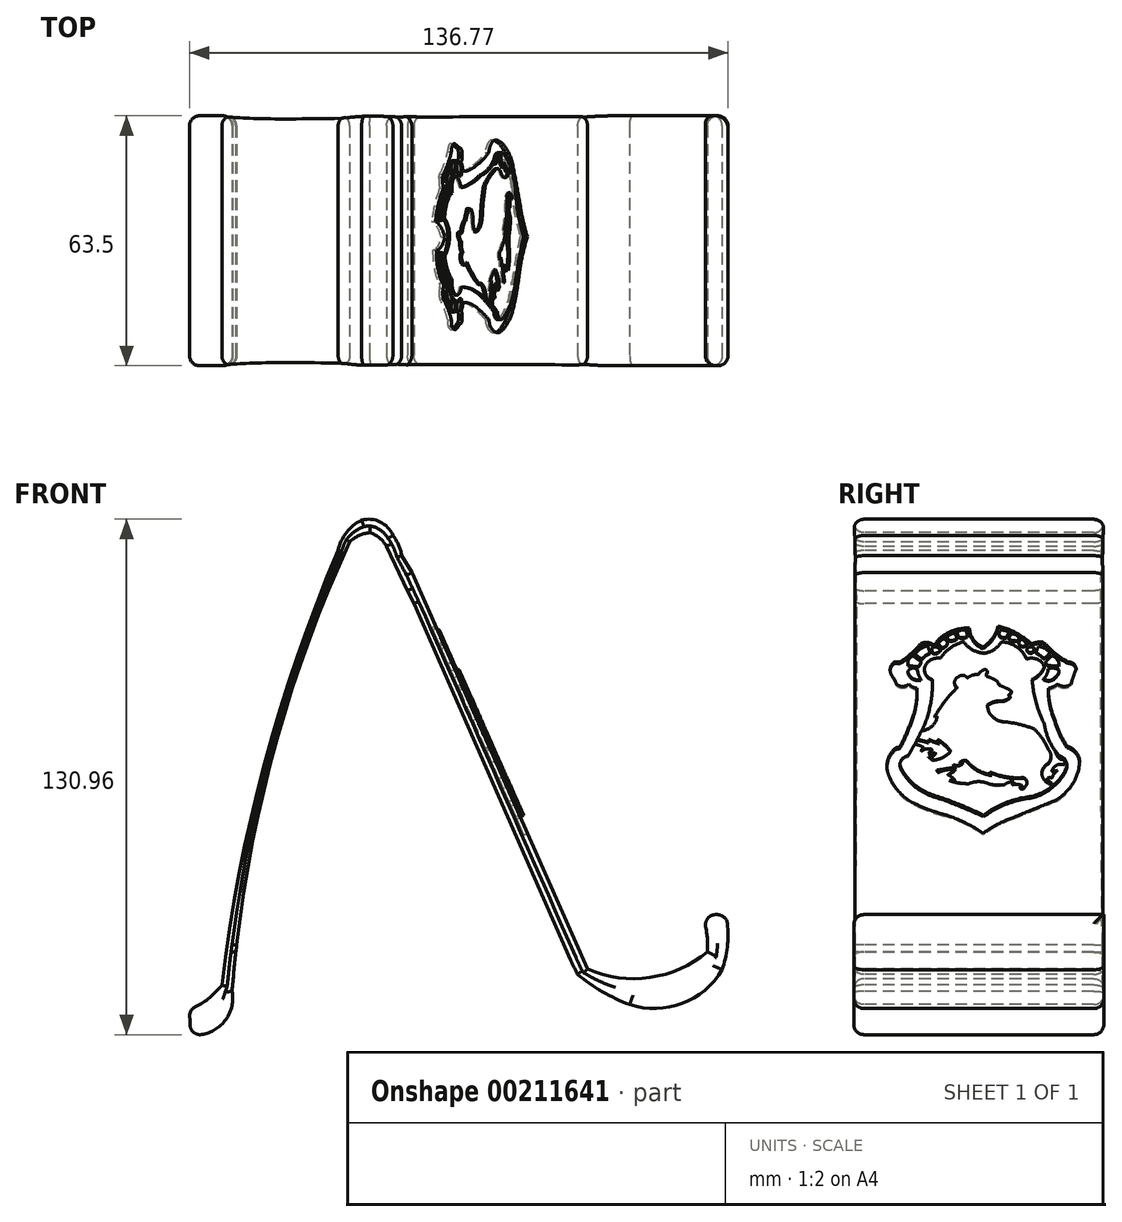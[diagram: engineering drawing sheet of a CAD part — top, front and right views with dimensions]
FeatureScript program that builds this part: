
annotation { "Feature Type Name" : "Feature", "Feature Type Description" : "" }
export const myFeature = defineFeature(function(context is Context, id is Id, definition is map)
    precondition{}
    {
        {
            var Q0;
            Q0=qCreatedBy(makeId("Front.planeOp"),FACE);
            var sketch = newSketch(context, id + "F0", { "sketchPlane" : qUnion([Q0])});
            skArc(sketch, "E0", {"start": v(-97.52, -51.49) * mm, "mid": v(-88.98, -49.1) * mm, "end": v(-86.27, -40.67) * mm});
            skArc(sketch, "E1", {"start": v(-56.41, 73.57) * mm, "mid": v(-76.4, 17.77) * mm, "end": v(-86.27, -40.67) * mm});
            skArc(sketch, "E2", {"start": v(-42.13, 67.94) * mm, "mid": v(-42.15, 68.13) * mm, "end": v(-42.16, 68.32) * mm});
            skArc(sketch, "E3", {"start": v(-0.28, -32.63) * mm, "mid": v(17.43, -37.36) * mm, "end": v(34.47, -30.58) * mm});
            skArc(sketch, "E4", {"start": v(34.47, -30.58) * mm, "mid": v(34.32, -25.84) * mm, "end": v(33.22, -21.21) * mm});
            skArc(sketch, "E5", {"start": v(39.25, -21.21) * mm, "mid": v(36.23, -21.14) * mm, "end": v(33.22, -21.21) * mm});
            skArc(sketch, "E6", {"start": v(1.53, -36.3) * mm, "mid": v(7.8, -40.71) * mm, "end": v(14.75, -44) * mm});
            skArc(sketch, "E7", {"start": v(-97.56, -45.4) * mm, "mid": v(-88.86, -39) * mm, "end": v(-85.13, -28.86) * mm});
            skArc(sketch, "E8", {"start": v(-97.52, -51.49) * mm, "mid": v(-96.94, -48.44) * mm, "end": v(-97.56, -45.4) * mm});
            skArc(sketch, "E9", {"start": v(-53.37, 79.07) * mm, "mid": v(-57.25, 75.9) * mm, "end": v(-59.32, 71.35) * mm});
            skArc(sketch, "E10", {"start": v(-59.32, 71.35) * mm, "mid": v(-78.06, 17.24) * mm, "end": v(-88.86, -39) * mm});
            skLineSegment(sketch, "E11", {"start": v(-97.52, -51.49) * mm, "end": v(-93.4, -51.49) * mm});
            skLineSegment(sketch, "E12", {"start": v(-86.19, -41.21) * mm, "end": v(-86.27, -40.67) * mm});
            skArc(sketch, "E13", {"start": v(38.22, -35.16) * mm, "mid": v(39.62, -28.25) * mm, "end": v(39.25, -21.21) * mm});
            skPoint(sketch, "E14.center.orphan", {"position": v(-0.28, -34.03) * mm});
            skPoint(sketch, "E15.start.orphan", {"position": v(39.25, -46.85) * mm});
            skArc(sketch, "E16", {"start": v(14.75, -44) * mm, "mid": v(28.05, -43.73) * mm, "end": v(38.22, -35.16) * mm});
            skPoint(sketch, "E17.orphan", {"position": v(30.56, -46.85) * mm});
            skLineSegment(sketch, "E18", {"start": v(-40.62, 65.75) * mm, "end": v(4, -34.96) * mm});
            skLineSegment(sketch, "E19", {"start": v(4, -34.96) * mm, "end": v(-0.28, -34.03) * mm});
            skLineSegment(sketch, "E20", {"start": v(-40.1, 57.85) * mm, "end": v(-0.28, -32.63) * mm});
            skArc(sketch, "E21", {"start": v(-0.28, -32.63) * mm, "mid": v(0.58, -34.49) * mm, "end": v(1.53, -36.3) * mm});
            skLineSegment(sketch, "E22", {"start": v(-41.73, 61.14) * mm, "end": v(-40.1, 57.85) * mm});
            skLineSegment(sketch, "E23", {"start": v(-41.73, 61.14) * mm, "end": v(-47.04, 72.42) * mm});
            skArc(sketch, "E24", {"start": v(-46.65, 71.6) * mm, "mid": v(-48.5, 74.28) * mm, "end": v(-51.32, 75.9) * mm});
            skPoint(sketch, "E25.orphan", {"position": v(-48.57, 75.7) * mm});
            skArc(sketch, "E26.trimOffspring", {"start": v(-51.32, 75.9) * mm, "mid": v(-54.06, 75.17) * mm, "end": v(-56.41, 73.57) * mm});
            skPoint(sketch, "E27.orphan", {"position": v(-59.32, 67.09) * mm});
            skArc(sketch, "E28", {"start": v(-45.43, 75.19) * mm, "mid": v(-48.66, 78.64) * mm, "end": v(-53.37, 79.07) * mm});
            skLineSegment(sketch, "E29.trimOffspring", {"start": v(-43.2, 70.06) * mm, "end": v(-40.62, 65.75) * mm});
            skPoint(sketch, "E30.orphan", {"position": v(-49.27, 80.15) * mm});
            skArc(sketch, "E31", {"start": v(-43.2, 70.06) * mm, "mid": v(-43.98, 72.77) * mm, "end": v(-45.43, 75.19) * mm});
            skPoint(sketch, "E32.orphan", {"position": v(-44.95, 72.95) * mm});
            skSolve(sketch);
        }
        {
            var Q0;
            Q0 = qSketchRegion(id + "F0", true);
            extrude(context, id + "F1", {"entities" : qUnion([Q0]), "oppositeDirection" : true, "depth" : 63.5 * mm});
        }
        {
            var Q0;
            Q0=makeQuery(id+"F1.opExtrude","SWEPT_FACE",FACE,{"disambiguationData":[OSD([sQuery(id+"F0.wireOp",EDGE,"E18")])]});
            var sketch = newSketch(context, id + "F2", { "sketchPlane" : qUnion([Q0])});
            skArc(sketch, "E33", {"start": v(29.4, 61.13) * mm, "mid": v(30.3, 58.01) * mm, "end": v(32.73, 55.87) * mm});
            skArc(sketch, "E34", {"start": v(32.73, 55.87) * mm, "mid": v(35.27, 58.44) * mm, "end": v(36.65, 61.78) * mm});
            skArc(sketch, "E35", {"start": v(45.1, 56.77) * mm, "mid": v(41.2, 59.83) * mm, "end": v(36.65, 61.78) * mm});
            skArc(sketch, "E36", {"start": v(47.95, 57.36) * mm, "mid": v(46.5, 57.23) * mm, "end": v(45.1, 56.77) * mm});
            skArc(sketch, "E37", {"start": v(47.95, 57.36) * mm, "mid": v(48.28, 56.98) * mm, "end": v(48.73, 56.77) * mm});
            skArc(sketch, "E38", {"start": v(48.73, 56.77) * mm, "mid": v(51.3, 53.95) * mm, "end": v(54.45, 51.76) * mm});
            skArc(sketch, "E39", {"start": v(56.47, 49.71) * mm, "mid": v(55.9, 51.16) * mm, "end": v(54.45, 51.76) * mm});
            skArc(sketch, "E40", {"start": v(56.47, 49.71) * mm, "mid": v(55.74, 47.66) * mm, "end": v(55.15, 45.55) * mm});
            skArc(sketch, "E41", {"start": v(51.75, 45.55) * mm, "mid": v(53.45, 44.95) * mm, "end": v(55.15, 45.55) * mm});
            skArc(sketch, "E42", {"start": v(49.39, 44.38) * mm, "mid": v(50.62, 44.87) * mm, "end": v(51.75, 45.55) * mm});
            skArc(sketch, "E43", {"start": v(49.39, 44.38) * mm, "mid": v(49.78, 40.1) * mm, "end": v(50.94, 35.98) * mm});
            skArc(sketch, "E44", {"start": v(50.94, 35.98) * mm, "mid": v(52.27, 32.04) * mm, "end": v(54.13, 28.34) * mm});
            skArc(sketch, "E45", {"start": v(57.36, 24.3) * mm, "mid": v(56.36, 26.81) * mm, "end": v(54.13, 28.34) * mm});
            skArc(sketch, "E46", {"start": v(51.39, 13.37) * mm, "mid": v(55.7, 18.12) * mm, "end": v(57.36, 24.3) * mm});
            skArc(sketch, "E47", {"start": v(51.39, 13.37) * mm, "mid": v(46, 10.96) * mm, "end": v(40.6, 8.54) * mm});
            skArc(sketch, "E48", {"start": v(40.6, 8.54) * mm, "mid": v(36.52, 6.66) * mm, "end": v(32.85, 4.1) * mm});
            skArc(sketch, "E49", {"start": v(32.85, 4.1) * mm, "mid": v(28.39, 7) * mm, "end": v(23.53, 9.18) * mm});
            skArc(sketch, "E50", {"start": v(15.99, 12.12) * mm, "mid": v(19.68, 10.46) * mm, "end": v(23.53, 9.18) * mm});
            skArc(sketch, "E51", {"start": v(9.07, 19.72) * mm, "mid": v(11.8, 15.25) * mm, "end": v(15.99, 12.12) * mm});
            skArc(sketch, "E52", {"start": v(10.14, 27.4) * mm, "mid": v(8.45, 23.73) * mm, "end": v(9.07, 19.72) * mm});
            skArc(sketch, "E53", {"start": v(11.62, 28) * mm, "mid": v(10.8, 27.9) * mm, "end": v(10.14, 27.4) * mm});
            skArc(sketch, "E54", {"start": v(11.62, 28) * mm, "mid": v(13.53, 32.42) * mm, "end": v(15.1, 36.97) * mm});
            skArc(sketch, "E55", {"start": v(15.1, 36.97) * mm, "mid": v(15.89, 40.68) * mm, "end": v(15.99, 44.46) * mm});
            skArc(sketch, "E56", {"start": v(13.98, 45.57) * mm, "mid": v(14.89, 44.84) * mm, "end": v(15.99, 44.46) * mm});
            skArc(sketch, "E57", {"start": v(10.77, 45.57) * mm, "mid": v(12.38, 44.96) * mm, "end": v(13.98, 45.57) * mm});
            skArc(sketch, "E58", {"start": v(10.77, 45.57) * mm, "mid": v(10.36, 46.75) * mm, "end": v(9.72, 47.84) * mm});
            skArc(sketch, "E59", {"start": v(10.14, 51.67) * mm, "mid": v(9.22, 49.83) * mm, "end": v(9.72, 47.84) * mm});
            skArc(sketch, "E60", {"start": v(11.62, 51.67) * mm, "mid": v(10.88, 51.75) * mm, "end": v(10.14, 51.67) * mm});
            skArc(sketch, "E61", {"start": v(11.62, 51.67) * mm, "mid": v(14.5, 54) * mm, "end": v(16.94, 56.82) * mm});
            skArc(sketch, "E62", {"start": v(19.78, 56.82) * mm, "mid": v(18.36, 57.21) * mm, "end": v(16.94, 56.82) * mm});
            skArc(sketch, "E63", {"start": v(19.78, 56.82) * mm, "mid": v(20.52, 56.62) * mm, "end": v(20.95, 57.25) * mm});
            skArc(sketch, "E64", {"start": v(29.4, 61.13) * mm, "mid": v(24.69, 60.24) * mm, "end": v(20.95, 57.25) * mm});
            skSolve(sketch);
        }
        {
            var Q0;
            Q0=makeQuery(id+"F2.imprint","IMPRINT",FACE,{"disambiguationData":[TD([[makeQuery(id+"F2.imprint","IMPRINT",EDGE,{"derivedFrom":sQuery(id+"F2.wireOp",EDGE,"E33")}),-1.0]])]});
            extrude(context, id + "F3", {"entities" : qUnion([Q0]), "operationType" : NewBodyOperationType.REMOVE, "oppositeDirection" : true, "depth" : 1.02 * mm});
        }
        {
            var Q0;
            Q0=makeQuery(id+"F2.imprint","IMPRINT",FACE,{"disambiguationData":[TD([[makeQuery(id+"F2.imprint","IMPRINT",EDGE,{"derivedFrom":sQuery(id+"F2.wireOp",EDGE,"E33")}),-1.0]])]});
            var sketch = newSketch(context, id + "F4", { "sketchPlane" : qUnion([Q0])});
            skArc(sketch, "E65", {"start": v(22, 52.6) * mm, "mid": v(19.59, 52.1) * mm, "end": v(18.03, 50.19) * mm});
            skArc(sketch, "E66", {"start": v(18.03, 50.19) * mm, "mid": v(18.29, 48.04) * mm, "end": v(19.95, 46.66) * mm});
            skArc(sketch, "E67", {"start": v(18.03, 34.27) * mm, "mid": v(19.57, 40.37) * mm, "end": v(19.95, 46.66) * mm});
            skArc(sketch, "E68", {"start": v(13.75, 25.22) * mm, "mid": v(16.01, 29.68) * mm, "end": v(18.03, 34.27) * mm});
            skArc(sketch, "E69", {"start": v(13.75, 25.22) * mm, "mid": v(11.99, 24) * mm, "end": v(12, 21.87) * mm});
            skArc(sketch, "E70", {"start": v(12, 21.87) * mm, "mid": v(15.77, 16.9) * mm, "end": v(21.26, 13.94) * mm});
            skArc(sketch, "E71", {"start": v(32.96, 8.68) * mm, "mid": v(27.2, 11.5) * mm, "end": v(21.26, 13.94) * mm});
            skArc(sketch, "E72", {"start": v(45.27, 13.94) * mm, "mid": v(38.72, 12.24) * mm, "end": v(32.96, 8.68) * mm});
            skArc(sketch, "E73", {"start": v(45.27, 13.94) * mm, "mid": v(50.53, 16.91) * mm, "end": v(53.98, 21.87) * mm});
            skArc(sketch, "E74", {"start": v(53.98, 21.87) * mm, "mid": v(53.84, 23.93) * mm, "end": v(52.22, 25.22) * mm});
            skArc(sketch, "E75", {"start": v(48.38, 34.27) * mm, "mid": v(49.7, 29.5) * mm, "end": v(52.22, 25.22) * mm});
            skArc(sketch, "E76", {"start": v(45.27, 46.66) * mm, "mid": v(46.28, 40.33) * mm, "end": v(48.38, 34.27) * mm});
            skArc(sketch, "E77", {"start": v(45.27, 46.66) * mm, "mid": v(47.15, 48.14) * mm, "end": v(48.38, 50.19) * mm});
            skArc(sketch, "E78", {"start": v(48.38, 50.19) * mm, "mid": v(46.61, 52.25) * mm, "end": v(43.9, 52.32) * mm});
            skArc(sketch, "E79", {"start": v(43.9, 52.32) * mm, "mid": v(41.37, 55.7) * mm, "end": v(37.41, 57.14) * mm});
            skArc(sketch, "E80", {"start": v(32.96, 53.95) * mm, "mid": v(35.6, 54.97) * mm, "end": v(37.41, 57.14) * mm});
            skArc(sketch, "E81", {"start": v(27.87, 57.14) * mm, "mid": v(30.05, 54.97) * mm, "end": v(32.96, 53.95) * mm});
            skArc(sketch, "E82", {"start": v(27.87, 57.14) * mm, "mid": v(24.5, 55.42) * mm, "end": v(22, 52.6) * mm});
            skArc(sketch, "E83", {"start": v(13.75, 48.96) * mm, "mid": v(14.81, 47) * mm, "end": v(17.03, 46.66) * mm});
            skArc(sketch, "E84", {"start": v(16.12, 49.45) * mm, "mid": v(14.81, 49.77) * mm, "end": v(13.75, 48.96) * mm});
            skArc(sketch, "E85", {"start": v(16.12, 49.45) * mm, "mid": v(16.42, 48) * mm, "end": v(17.03, 46.66) * mm});
            skArc(sketch, "E86", {"start": v(13.75, 50.6) * mm, "mid": v(15, 50.35) * mm, "end": v(16.25, 50.19) * mm});
            skArc(sketch, "E87", {"start": v(15.05, 53.2) * mm, "mid": v(16.02, 52.43) * mm, "end": v(17.03, 51.7) * mm});
            skArc(sketch, "E88", {"start": v(16.25, 50.19) * mm, "mid": v(16.8, 50.86) * mm, "end": v(17.03, 51.7) * mm});
            skArc(sketch, "E89", {"start": v(15.05, 53.2) * mm, "mid": v(13.9, 52.15) * mm, "end": v(13.75, 50.6) * mm});
            skArc(sketch, "E90", {"start": v(15.64, 53.95) * mm, "mid": v(16.35, 52.98) * mm, "end": v(17.36, 52.32) * mm});
            skArc(sketch, "E91", {"start": v(19.32, 53.95) * mm, "mid": v(19.07, 55) * mm, "end": v(18.7, 56) * mm});
            skArc(sketch, "E92", {"start": v(18.7, 56) * mm, "mid": v(17.02, 55.21) * mm, "end": v(15.64, 53.95) * mm});
            skArc(sketch, "E93", {"start": v(19.32, 53.95) * mm, "mid": v(18.17, 53.35) * mm, "end": v(17.36, 52.32) * mm});
            skArc(sketch, "E94", {"start": v(22, 54.78) * mm, "mid": v(21.13, 55.58) * mm, "end": v(19.95, 55.47) * mm});
            skArc(sketch, "E95", {"start": v(19.95, 55.47) * mm, "mid": v(19.8, 54.83) * mm, "end": v(19.95, 54.2) * mm});
            skArc(sketch, "E96", {"start": v(20.86, 53.95) * mm, "mid": v(21.49, 54.3) * mm, "end": v(22, 54.78) * mm});
            skArc(sketch, "E97", {"start": v(19.95, 54.2) * mm, "mid": v(20.37, 53.94) * mm, "end": v(20.86, 53.95) * mm});
            skArc(sketch, "E98", {"start": v(21.49, 56.69) * mm, "mid": v(21.9, 55.98) * mm, "end": v(22.54, 55.47) * mm});
            skArc(sketch, "E99", {"start": v(22.54, 55.47) * mm, "mid": v(23.45, 56.1) * mm, "end": v(23.82, 57.14) * mm});
            skArc(sketch, "E100", {"start": v(22.98, 57.93) * mm, "mid": v(22.09, 57.48) * mm, "end": v(21.49, 56.69) * mm});
            skArc(sketch, "E101", {"start": v(22.98, 57.93) * mm, "mid": v(23.4, 57.52) * mm, "end": v(23.82, 57.14) * mm});
            skArc(sketch, "E102", {"start": v(23.82, 58.6) * mm, "mid": v(23.94, 57.87) * mm, "end": v(24.55, 57.45) * mm});
            skArc(sketch, "E103", {"start": v(24.55, 57.45) * mm, "mid": v(25.36, 57.58) * mm, "end": v(26.11, 57.93) * mm});
            skArc(sketch, "E104", {"start": v(26.11, 57.93) * mm, "mid": v(25.94, 58.8) * mm, "end": v(25.46, 59.55) * mm});
            skArc(sketch, "E105", {"start": v(25.46, 59.55) * mm, "mid": v(24.58, 59.19) * mm, "end": v(23.82, 58.6) * mm});
            skArc(sketch, "E106", {"start": v(26.36, 59.83) * mm, "mid": v(26.41, 58.98) * mm, "end": v(26.95, 58.32) * mm});
            skArc(sketch, "E107", {"start": v(26.95, 58.32) * mm, "mid": v(27.9, 58.3) * mm, "end": v(28.8, 58.6) * mm});
            skArc(sketch, "E108", {"start": v(28.8, 58.6) * mm, "mid": v(28.7, 59.48) * mm, "end": v(28.43, 60.32) * mm});
            skArc(sketch, "E109", {"start": v(28.43, 60.32) * mm, "mid": v(27.33, 60.36) * mm, "end": v(26.36, 59.83) * mm});
            skArc(sketch, "E110", {"start": v(37.15, 60.32) * mm, "mid": v(36.9, 59.47) * mm, "end": v(37.06, 58.6) * mm});
            skArc(sketch, "E111", {"start": v(39.35, 59.83) * mm, "mid": v(38.3, 60.3) * mm, "end": v(37.15, 60.32) * mm});
            skArc(sketch, "E112", {"start": v(37.06, 58.6) * mm, "mid": v(37.86, 58.33) * mm, "end": v(38.71, 58.32) * mm});
            skArc(sketch, "E113", {"start": v(38.71, 58.32) * mm, "mid": v(39.1, 59.05) * mm, "end": v(39.35, 59.83) * mm});
            skArc(sketch, "E114", {"start": v(40.17, 59.37) * mm, "mid": v(39.63, 58.73) * mm, "end": v(39.35, 57.93) * mm});
            skArc(sketch, "E115", {"start": v(39.35, 57.93) * mm, "mid": v(40.11, 57.54) * mm, "end": v(40.96, 57.45) * mm});
            skArc(sketch, "E116", {"start": v(41.89, 58.32) * mm, "mid": v(41.14, 59.03) * mm, "end": v(40.17, 59.37) * mm});
            skArc(sketch, "E117", {"start": v(40.96, 57.45) * mm, "mid": v(41.69, 57.6) * mm, "end": v(41.89, 58.32) * mm});
            skArc(sketch, "E118", {"start": v(42.6, 57.93) * mm, "mid": v(42.14, 57.37) * mm, "end": v(41.89, 56.69) * mm});
            skArc(sketch, "E119", {"start": v(43.93, 56.32) * mm, "mid": v(43.36, 57.2) * mm, "end": v(42.6, 57.93) * mm});
            skArc(sketch, "E120", {"start": v(42.88, 55.84) * mm, "mid": v(43.44, 56) * mm, "end": v(43.93, 56.32) * mm});
            skArc(sketch, "E121", {"start": v(41.89, 56.69) * mm, "mid": v(42.3, 56.18) * mm, "end": v(42.88, 55.84) * mm});
            skArc(sketch, "E122", {"start": v(45.63, 55.59) * mm, "mid": v(44.64, 55.64) * mm, "end": v(43.93, 54.93) * mm});
            skArc(sketch, "E123", {"start": v(45.08, 54.1) * mm, "mid": v(45.69, 54.73) * mm, "end": v(45.63, 55.59) * mm});
            skArc(sketch, "E124", {"start": v(43.93, 54.93) * mm, "mid": v(44.37, 54.32) * mm, "end": v(45.08, 54.1) * mm});
            skArc(sketch, "E125", {"start": v(46.94, 55.84) * mm, "mid": v(46.53, 55) * mm, "end": v(46.25, 54.1) * mm});
            skArc(sketch, "E126", {"start": v(49.79, 54.1) * mm, "mid": v(48.54, 55.26) * mm, "end": v(46.94, 55.84) * mm});
            skArc(sketch, "E127", {"start": v(48.19, 52.53) * mm, "mid": v(47.3, 53.42) * mm, "end": v(46.25, 54.1) * mm});
            skArc(sketch, "E128", {"start": v(48.19, 52.53) * mm, "mid": v(49.1, 53.2) * mm, "end": v(49.79, 54.1) * mm});
            skArc(sketch, "E129", {"start": v(50.41, 53.24) * mm, "mid": v(49.53, 52.49) * mm, "end": v(48.8, 51.59) * mm});
            skArc(sketch, "E130", {"start": v(52.14, 50.5) * mm, "mid": v(51.7, 52.14) * mm, "end": v(50.41, 53.24) * mm});
            skArc(sketch, "E131", {"start": v(49.32, 50.64) * mm, "mid": v(50.72, 50.43) * mm, "end": v(52.14, 50.5) * mm});
            skArc(sketch, "E132", {"start": v(48.8, 51.59) * mm, "mid": v(48.89, 51.02) * mm, "end": v(49.32, 50.64) * mm});
            skArc(sketch, "E133", {"start": v(48.19, 46.78) * mm, "mid": v(49.01, 48.08) * mm, "end": v(49.32, 49.58) * mm});
            skArc(sketch, "E134", {"start": v(48.19, 46.78) * mm, "mid": v(49.86, 46.43) * mm, "end": v(51.25, 47.43) * mm});
            skArc(sketch, "E135", {"start": v(51.25, 47.43) * mm, "mid": v(51.89, 48.24) * mm, "end": v(52.14, 49.24) * mm});
            skArc(sketch, "E136", {"start": v(52.14, 49.24) * mm, "mid": v(50.77, 49.8) * mm, "end": v(49.32, 49.58) * mm});
            skSolve(sketch);
        }
        {
            var Q0;
            Q0 = qSketchRegion(id + "F4", true);
            extrude(context, id + "F5", {"entities" : qUnion([Q0]), "depth" : 0.5 * mm});
        }
        {
            var Q0;
            Q0=makeQuery(id+"F5.opExtrude","CAP_FACE",FACE,{"disambiguationData":[OSD([sQuery(id+"F4.wireOp",EDGE,"E65"),sQuery(id+"F4.wireOp",EDGE,"E66"),sQuery(id+"F4.wireOp",EDGE,"E67"),sQuery(id+"F4.wireOp",EDGE,"E68"),sQuery(id+"F4.wireOp",EDGE,"E69"),sQuery(id+"F4.wireOp",EDGE,"E70"),sQuery(id+"F4.wireOp",EDGE,"E71"),sQuery(id+"F4.wireOp",EDGE,"E72"),sQuery(id+"F4.wireOp",EDGE,"E73"),sQuery(id+"F4.wireOp",EDGE,"E74"),sQuery(id+"F4.wireOp",EDGE,"E75"),sQuery(id+"F4.wireOp",EDGE,"E76"),sQuery(id+"F4.wireOp",EDGE,"E77"),sQuery(id+"F4.wireOp",EDGE,"E78"),sQuery(id+"F4.wireOp",EDGE,"E79"),sQuery(id+"F4.wireOp",EDGE,"E80"),sQuery(id+"F4.wireOp",EDGE,"E81"),sQuery(id+"F4.wireOp",EDGE,"E82")])],"isStart":false});
            var sketch = newSketch(context, id + "F6", { "sketchPlane" : qUnion([Q0])});
            skArc(sketch, "E137", {"start": v(26.28, 44.17) * mm, "mid": v(23.12, 40.38) * mm, "end": v(20.58, 36.14) * mm});
            skArc(sketch, "E138", {"start": v(17.14, 32.16) * mm, "mid": v(19.86, 33.48) * mm, "end": v(21.12, 36.23) * mm});
            skLineSegment(sketch, "E139", {"start": v(20.58, 36.14) * mm, "end": v(21.12, 36.23) * mm});
            skArc(sketch, "E140", {"start": v(24.58, 26.44) * mm, "mid": v(23.12, 28.31) * mm, "end": v(21.23, 29.76) * mm});
            skArc(sketch, "E141", {"start": v(19.12, 29.76) * mm, "mid": v(20.4, 29.2) * mm, "end": v(21.72, 28.7) * mm});
            skArc(sketch, "E142", {"start": v(18.87, 28.95) * mm, "mid": v(17.48, 29.46) * mm, "end": v(16.01, 29.68) * mm});
            skLineSegment(sketch, "E143", {"start": v(19.12, 29.76) * mm, "end": v(18.87, 28.95) * mm});
            skLineSegment(sketch, "E144", {"start": v(21.23, 29.76) * mm, "end": v(21.72, 28.7) * mm});
            skArc(sketch, "E145", {"start": v(19.88, 24) * mm, "mid": v(22.5, 24.7) * mm, "end": v(24.58, 26.44) * mm});
            skArc(sketch, "E146", {"start": v(19.88, 24) * mm, "mid": v(19.44, 24.44) * mm, "end": v(18.96, 24.83) * mm});
            skArc(sketch, "E147", {"start": v(18.96, 24.83) * mm, "mid": v(20.06, 25.19) * mm, "end": v(20.74, 26.12) * mm});
            skArc(sketch, "E148", {"start": v(18.96, 25.87) * mm, "mid": v(19.86, 25.9) * mm, "end": v(20.74, 26.12) * mm});
            skArc(sketch, "E149", {"start": v(19.88, 26.99) * mm, "mid": v(19.42, 26.43) * mm, "end": v(18.96, 25.87) * mm});
            skArc(sketch, "E150", {"start": v(19.88, 26.99) * mm, "mid": v(18.42, 27.14) * mm, "end": v(17.12, 26.44) * mm});
            skArc(sketch, "E151", {"start": v(17.7, 27.52) * mm, "mid": v(17.28, 27.05) * mm, "end": v(17.12, 26.44) * mm});
            skArc(sketch, "E152", {"start": v(17.7, 27.52) * mm, "mid": v(16.6, 28.11) * mm, "end": v(15.4, 28.4) * mm});
            skArc(sketch, "E153", {"start": v(28.75, 23.75) * mm, "mid": v(31.55, 21.19) * mm, "end": v(35.12, 19.94) * mm});
            skArc(sketch, "E154", {"start": v(34.5, 20.81) * mm, "mid": v(38.64, 19.38) * mm, "end": v(43.01, 19.17) * mm});
            skArc(sketch, "E155", {"start": v(43.46, 16.67) * mm, "mid": v(43.96, 18.05) * mm, "end": v(43.01, 19.17) * mm});
            skArc(sketch, "E156", {"start": v(42.16, 16.3) * mm, "mid": v(42.94, 16.05) * mm, "end": v(43.46, 16.67) * mm});
            skArc(sketch, "E157", {"start": v(42.74, 17) * mm, "mid": v(42.4, 16.7) * mm, "end": v(42.16, 16.3) * mm});
            skArc(sketch, "E158", {"start": v(42.74, 17) * mm, "mid": v(41.5, 17.27) * mm, "end": v(40.25, 17.16) * mm});
            skArc(sketch, "E159", {"start": v(40.61, 17.92) * mm, "mid": v(40.28, 17.6) * mm, "end": v(40.25, 17.16) * mm});
            skArc(sketch, "E160", {"start": v(40.61, 17.92) * mm, "mid": v(39.32, 17.82) * mm, "end": v(38.2, 17.16) * mm});
            skArc(sketch, "E161", {"start": v(34.2, 17.45) * mm, "mid": v(36.19, 17.09) * mm, "end": v(38.2, 17.16) * mm});
            skArc(sketch, "E162", {"start": v(34.2, 17.45) * mm, "mid": v(31.7, 18.05) * mm, "end": v(29.19, 17.45) * mm});
            skArc(sketch, "E163", {"start": v(24.23, 18.38) * mm, "mid": v(26.66, 17.66) * mm, "end": v(29.19, 17.45) * mm});
            skArc(sketch, "E164", {"start": v(25.65, 18.38) * mm, "mid": v(24.94, 18.45) * mm, "end": v(24.23, 18.38) * mm});
            skArc(sketch, "E165", {"start": v(25.65, 18.38) * mm, "mid": v(24.87, 19.31) * mm, "end": v(23.82, 19.94) * mm});
            skArc(sketch, "E166", {"start": v(23.82, 19.94) * mm, "mid": v(24.75, 20.57) * mm, "end": v(25.65, 21.25) * mm});
            skLineSegment(sketch, "E167", {"start": v(34.5, 20.81) * mm, "end": v(35.12, 19.94) * mm});
            skArc(sketch, "E168", {"start": v(25.65, 21.25) * mm, "mid": v(23.52, 21.3) * mm, "end": v(21.52, 20.56) * mm});
            skArc(sketch, "E169", {"start": v(21.1, 21.25) * mm, "mid": v(21.2, 20.83) * mm, "end": v(21.52, 20.56) * mm});
            skArc(sketch, "E170", {"start": v(21.1, 21.25) * mm, "mid": v(23.56, 21.66) * mm, "end": v(26, 22.16) * mm});
            skArc(sketch, "E171", {"start": v(25.23, 22.75) * mm, "mid": v(26.47, 22.6) * mm, "end": v(27.6, 23.15) * mm});
            skArc(sketch, "E172", {"start": v(28.37, 23.96) * mm, "mid": v(27.5, 23.8) * mm, "end": v(26.78, 23.32) * mm});
            skArc(sketch, "E173", {"start": v(28.75, 23.75) * mm, "mid": v(28.6, 23.92) * mm, "end": v(28.37, 23.96) * mm});
            skLineSegment(sketch, "E174", {"start": v(26.78, 23.32) * mm, "end": v(27.6, 23.15) * mm});
            skLineSegment(sketch, "E175", {"start": v(25.23, 22.75) * mm, "end": v(26, 22.16) * mm});
            skPoint(sketch, "E176.endSnap0", {"position": v(50.53, 16.91) * mm});
            skPoint(sketch, "E176.start.orphan", {"position": v(49.4, 23.15) * mm});
            skPoint(sketch, "E177.start.orphan", {"position": v(50.53, 17.37) * mm});
            skArc(sketch, "E178", {"start": v(49.4, 23.15) * mm, "mid": v(47.76, 20.36) * mm, "end": v(49.4, 17.58) * mm});
            skArc(sketch, "E179", {"start": v(49.4, 23.15) * mm, "mid": v(50.06, 25.09) * mm, "end": v(49.4, 27.02) * mm});
            skArc(sketch, "E180", {"start": v(49.4, 27.02) * mm, "mid": v(47.88, 30) * mm, "end": v(45.83, 32.67) * mm});
            skArc(sketch, "E181", {"start": v(45.83, 32.67) * mm, "mid": v(42.14, 33.94) * mm, "end": v(38.3, 34.65) * mm});
            skArc(sketch, "E182", {"start": v(33.98, 39.35) * mm, "mid": v(35.16, 36.1) * mm, "end": v(38.3, 34.65) * mm});
            skArc(sketch, "E183", {"start": v(49.2, 19.02) * mm, "mid": v(49.63, 18.2) * mm, "end": v(50.31, 17.58) * mm});
            skArc(sketch, "E184", {"start": v(50.32, 19.02) * mm, "mid": v(49.76, 19.15) * mm, "end": v(49.2, 19.02) * mm});
            skArc(sketch, "E185", {"start": v(51.68, 21.14) * mm, "mid": v(50.83, 20.18) * mm, "end": v(50.32, 19.02) * mm});
            skArc(sketch, "E186", {"start": v(50.32, 21.14) * mm, "mid": v(51, 20.95) * mm, "end": v(51.68, 21.14) * mm});
            skArc(sketch, "E187", {"start": v(53.37, 22.73) * mm, "mid": v(51.5, 22.6) * mm, "end": v(50.32, 21.14) * mm});
            skArc(sketch, "E188", {"start": v(53.37, 22.73) * mm, "mid": v(53.58, 23.5) * mm, "end": v(53.37, 24.29) * mm});
            skArc(sketch, "E189", {"start": v(53.37, 24.29) * mm, "mid": v(53.03, 24.52) * mm, "end": v(52.7, 24.29) * mm});
            skArc(sketch, "E190", {"start": v(51.2, 26.67) * mm, "mid": v(51.7, 25.33) * mm, "end": v(52.7, 24.29) * mm});
            skArc(sketch, "E191", {"start": v(49.4, 17.58) * mm, "mid": v(49.86, 17.4) * mm, "end": v(50.31, 17.58) * mm});
            skArc(sketch, "E192", {"start": v(26.72, 47.27) * mm, "mid": v(25.59, 45.85) * mm, "end": v(26.28, 44.17) * mm});
            skArc(sketch, "E193", {"start": v(28.82, 46.8) * mm, "mid": v(27.9, 47.58) * mm, "end": v(26.72, 47.27) * mm});
            skArc(sketch, "E194", {"start": v(31.6, 47.78) * mm, "mid": v(30.1, 47.6) * mm, "end": v(28.82, 46.8) * mm});
            skArc(sketch, "E195", {"start": v(33.28, 49.2) * mm, "mid": v(32.3, 48.66) * mm, "end": v(31.6, 47.78) * mm});
            skArc(sketch, "E196", {"start": v(33.75, 48.16) * mm, "mid": v(33.84, 48.84) * mm, "end": v(33.28, 49.2) * mm});
            skArc(sketch, "E197", {"start": v(33.7, 48.1) * mm, "mid": v(33.62, 47.68) * mm, "end": v(33.75, 47.27) * mm});
            skArc(sketch, "E198", {"start": v(36.86, 45.4) * mm, "mid": v(35.44, 46.56) * mm, "end": v(33.75, 47.27) * mm});
            skArc(sketch, "E199", {"start": v(36.86, 45.4) * mm, "mid": v(36.8, 45.01) * mm, "end": v(37.11, 44.78) * mm});
            skArc(sketch, "E200", {"start": v(39.92, 43.36) * mm, "mid": v(38.53, 44.09) * mm, "end": v(37.11, 44.78) * mm});
            skArc(sketch, "E201", {"start": v(39.4, 42.23) * mm, "mid": v(39.88, 42.7) * mm, "end": v(39.92, 43.36) * mm});
            skArc(sketch, "E202", {"start": v(39.4, 42.23) * mm, "mid": v(39.4, 41.83) * mm, "end": v(39.74, 41.6) * mm});
            skArc(sketch, "E203", {"start": v(37.4, 40.48) * mm, "mid": v(35.57, 40.26) * mm, "end": v(33.98, 39.35) * mm});
            skArc(sketch, "E204", {"start": v(37.4, 40.48) * mm, "mid": v(38.68, 40.8) * mm, "end": v(39.74, 41.6) * mm});
            skArc(sketch, "E205", {"start": v(16.01, 29.68) * mm, "mid": v(16.6, 30.9) * mm, "end": v(17.14, 32.16) * mm});
            skArc(sketch, "E206", {"start": v(13.75, 25.22) * mm, "mid": v(14.6, 26.8) * mm, "end": v(15.4, 28.4) * mm});
            skArc(sketch, "E207", {"start": v(13.75, 25.22) * mm, "mid": v(11.81, 23.48) * mm, "end": v(12.46, 20.96) * mm});
            skArc(sketch, "E208", {"start": v(12.46, 20.96) * mm, "mid": v(16.15, 16.44) * mm, "end": v(21.4, 13.89) * mm});
            skArc(sketch, "E209", {"start": v(32.96, 8.68) * mm, "mid": v(27.26, 11.47) * mm, "end": v(21.4, 13.89) * mm});
            skArc(sketch, "E210", {"start": v(45.27, 13.94) * mm, "mid": v(38.74, 12.2) * mm, "end": v(32.96, 8.68) * mm});
            skArc(sketch, "E211", {"start": v(45.27, 13.94) * mm, "mid": v(50.53, 16.91) * mm, "end": v(53.98, 21.87) * mm});
            skArc(sketch, "E212", {"start": v(53.98, 21.87) * mm, "mid": v(53.8, 23.91) * mm, "end": v(52.22, 25.22) * mm});
            skArc(sketch, "E213", {"start": v(51.2, 26.67) * mm, "mid": v(51.65, 25.9) * mm, "end": v(52.22, 25.22) * mm});
            skLineSegment(sketch, "E214", {"start": v(33.75, 48.16) * mm, "end": v(33.7, 48.1) * mm});
            skSolve(sketch);
        }
        {
            var Q0;
            Q0=makeQuery(id+"F6.imprint","IMPRINT",FACE,{"disambiguationData":[TD([[makeQuery(id+"F6.imprint","IMPRINT",EDGE,{"derivedFrom":sQuery(id+"F6.wireOp",EDGE,"E137")}),1.0]])]});
            extrude(context, id + "F7", {"entities" : qUnion([Q0]), "depth" : 0.5 * mm});
        }
        {
            var Q0;
            Q0=makeQuery(id+"F1.opExtrude","CAP_EDGE",EDGE,{"disambiguationData":[OSD([sQuery(id+"F0.wireOp",EDGE,"E0")])],"isStart":true});
            var Q1;
            Q1=makeQuery(id+"F1.opExtrude","SWEPT_EDGE",EDGE,{"disambiguationData":[OSD([sQuery(id+"F0.wireOp",EDGE,"E0"),sQuery(id+"F0.wireOp",EDGE,"E8"),sQuery(id+"F0.wireOp",EDGE,"E11")])]});
            var Q2;
            Q2=makeQuery(id+"F1.opExtrude","SWEPT_EDGE",EDGE,{"disambiguationData":[OSD([sQuery(id+"F0.wireOp",EDGE,"E7"),sQuery(id+"F0.wireOp",EDGE,"E8")])]});
            var Q3;
            {var subQ0=sQuery(id+"F0.wireOp",EDGE,"E7");Q3=makeQuery(id+"F1.opExtrude","CAP_EDGE",EDGE,{"disambiguationData":[OSD([subQ0]),TDD([makeQuery(id+"F0.imprint","IMPRINT",EDGE,{"disambiguationData":[TD([[makeQuery(id+"F0.imprint","INTERSECT",VERTEX,{"derivedFrom":[subQ0,sQuery(id+"F0.wireOp",EDGE,"E8")]}),-1.0]])],"derivedFrom":subQ0})])],"isStart":true});}
            var Q4;
            Q4=makeQuery(id+"F1.opExtrude","CAP_EDGE",EDGE,{"disambiguationData":[OSD([sQuery(id+"F0.wireOp",EDGE,"E10")])],"isStart":true});
            var Q5;
            {var subQ0=sQuery(id+"F0.wireOp",EDGE,"E1");Q5=makeQuery(id+"F1.opExtrude","CAP_EDGE",EDGE,{"disambiguationData":[OSD([subQ0]),TDD([makeQuery(id+"F0.imprint","IMPRINT",EDGE,{"disambiguationData":[TD([[makeQuery(id+"F0.imprint","INTERSECT",VERTEX,{"derivedFrom":[subQ0,sQuery(id+"F0.wireOp",EDGE,"E26.trimOffspring")]}),-1.0]])],"derivedFrom":subQ0})])],"isStart":true});}
            var Q6;
            {var subQ0=sQuery(id+"F0.wireOp",EDGE,"E1");Q6=makeQuery(id+"F1.opExtrude","CAP_EDGE",EDGE,{"disambiguationData":[OSD([subQ0]),TDD([makeQuery(id+"F0.imprint","IMPRINT",EDGE,{"disambiguationData":[TD([[makeQuery(id+"F0.imprint","INTERSECT",VERTEX,{"disambiguationData":[OD(1.0)],"derivedFrom":[subQ0,sQuery(id+"F0.wireOp",EDGE,"E7")]}),-1.0]])],"derivedFrom":subQ0})])],"isStart":true});}
            var Q7;
            {var subQ0=sQuery(id+"F0.wireOp",EDGE,"E7");var subQ1=sQuery(id+"F0.wireOp",EDGE,"E1");Q7=makeQuery(id+"F1.opExtrude","CAP_EDGE",EDGE,{"disambiguationData":[OSD([subQ0]),TDD([makeQuery(id+"F0.imprint","IMPRINT",EDGE,{"disambiguationData":[TD([[makeQuery(id+"F0.imprint","INTERSECT",VERTEX,{"disambiguationData":[OD(0.0)],"derivedFrom":[subQ1,subQ0]}),1.0]])],"derivedFrom":subQ0})])],"isStart":true});}
            var Q8;
            Q8=makeQuery(id+"F1.opExtrude","CAP_EDGE",EDGE,{"disambiguationData":[OSD([sQuery(id+"F0.wireOp",EDGE,"E26.trimOffspring")])],"isStart":true});
            var Q9;
            Q9=makeQuery(id+"F1.opExtrude","CAP_EDGE",EDGE,{"disambiguationData":[OSD([sQuery(id+"F0.wireOp",EDGE,"E9")])],"isStart":true});
            var Q10;
            Q10=makeQuery(id+"F1.opExtrude","CAP_EDGE",EDGE,{"disambiguationData":[OSD([sQuery(id+"F0.wireOp",EDGE,"E28")])],"isStart":true});
            var Q11;
            Q11=makeQuery(id+"F1.opExtrude","CAP_EDGE",EDGE,{"disambiguationData":[OSD([sQuery(id+"F0.wireOp",EDGE,"E20")])],"isStart":true});
            var Q12;
            Q12=makeQuery(id+"F1.opExtrude","CAP_EDGE",EDGE,{"disambiguationData":[OSD([sQuery(id+"F0.wireOp",EDGE,"E23")])],"isStart":true});
            var Q13;
            Q13=makeQuery(id+"F1.opExtrude","CAP_EDGE",EDGE,{"disambiguationData":[OSD([sQuery(id+"F0.wireOp",EDGE,"E22")])],"isStart":true});
            var Q14;
            Q14=makeQuery(id+"F1.opExtrude","CAP_EDGE",EDGE,{"disambiguationData":[OSD([sQuery(id+"F0.wireOp",EDGE,"E24")])],"isStart":true});
            var Q15;
            Q15=makeQuery(id+"F1.opExtrude","CAP_EDGE",EDGE,{"disambiguationData":[OSD([sQuery(id+"F0.wireOp",EDGE,"E31")])],"isStart":true});
            var Q16;
            Q16=makeQuery(id+"F1.opExtrude","CAP_EDGE",EDGE,{"disambiguationData":[OSD([sQuery(id+"F0.wireOp",EDGE,"E29.trimOffspring")])],"isStart":true});
            var Q17;
            Q17=makeQuery(id+"F1.opExtrude","CAP_EDGE",EDGE,{"disambiguationData":[OSD([sQuery(id+"F0.wireOp",EDGE,"E18")])],"isStart":true});
            var Q18;
            Q18=makeQuery(id+"F1.opExtrude","CAP_EDGE",EDGE,{"disambiguationData":[OSD([sQuery(id+"F0.wireOp",EDGE,"E21")])],"isStart":true});
            var Q19;
            Q19=makeQuery(id+"F1.opExtrude","CAP_EDGE",EDGE,{"disambiguationData":[OSD([sQuery(id+"F0.wireOp",EDGE,"E6")])],"isStart":true});
            var Q20;
            Q20=makeQuery(id+"F1.opExtrude","CAP_EDGE",EDGE,{"disambiguationData":[OSD([sQuery(id+"F0.wireOp",EDGE,"E16")])],"isStart":true});
            var Q21;
            Q21=makeQuery(id+"F1.opExtrude","CAP_EDGE",EDGE,{"disambiguationData":[OSD([sQuery(id+"F0.wireOp",EDGE,"E13")])],"isStart":true});
            var Q22;
            Q22=makeQuery(id+"F1.opExtrude","CAP_EDGE",EDGE,{"disambiguationData":[OSD([sQuery(id+"F0.wireOp",EDGE,"E3")])],"isStart":true});
            var Q23;
            Q23=makeQuery(id+"F1.opExtrude","CAP_EDGE",EDGE,{"disambiguationData":[OSD([sQuery(id+"F0.wireOp",EDGE,"E4")])],"isStart":true});
            var Q24;
            Q24=makeQuery(id+"F1.opExtrude","CAP_EDGE",EDGE,{"disambiguationData":[OSD([sQuery(id+"F0.wireOp",EDGE,"E5")])],"isStart":true});
            var Q25;
            Q25=makeQuery(id+"F1.opExtrude","SWEPT_EDGE",EDGE,{"disambiguationData":[OSD([sQuery(id+"F0.wireOp",EDGE,"E5"),sQuery(id+"F0.wireOp",EDGE,"E13")])]});
            var Q26;
            Q26=makeQuery(id+"F1.opExtrude","SWEPT_EDGE",EDGE,{"disambiguationData":[OSD([sQuery(id+"F0.wireOp",EDGE,"E4"),sQuery(id+"F0.wireOp",EDGE,"E5")])]});
            var Q27;
            Q27=makeQuery(id+"F1.opExtrude","CAP_EDGE",EDGE,{"disambiguationData":[OSD([sQuery(id+"F0.wireOp",EDGE,"E3")])],"isStart":false});
            var Q28;
            Q28=makeQuery(id+"F1.opExtrude","CAP_EDGE",EDGE,{"disambiguationData":[OSD([sQuery(id+"F0.wireOp",EDGE,"E4")])],"isStart":false});
            var Q29;
            Q29=makeQuery(id+"F1.opExtrude","CAP_EDGE",EDGE,{"disambiguationData":[OSD([sQuery(id+"F0.wireOp",EDGE,"E13")])],"isStart":false});
            var Q30;
            Q30=makeQuery(id+"F1.opExtrude","CAP_EDGE",EDGE,{"disambiguationData":[OSD([sQuery(id+"F0.wireOp",EDGE,"E16")])],"isStart":false});
            var Q31;
            Q31=makeQuery(id+"F1.opExtrude","CAP_EDGE",EDGE,{"disambiguationData":[OSD([sQuery(id+"F0.wireOp",EDGE,"E6")])],"isStart":false});
            var Q32;
            Q32=makeQuery(id+"F1.opExtrude","CAP_EDGE",EDGE,{"disambiguationData":[OSD([sQuery(id+"F0.wireOp",EDGE,"E20")])],"isStart":false});
            var Q33;
            Q33=makeQuery(id+"F1.opExtrude","CAP_EDGE",EDGE,{"disambiguationData":[OSD([sQuery(id+"F0.wireOp",EDGE,"E21")])],"isStart":false});
            var Q34;
            Q34=makeQuery(id+"F1.opExtrude","CAP_EDGE",EDGE,{"disambiguationData":[OSD([sQuery(id+"F0.wireOp",EDGE,"E18")])],"isStart":false});
            var Q35;
            Q35=makeQuery(id+"F1.opExtrude","CAP_EDGE",EDGE,{"disambiguationData":[OSD([sQuery(id+"F0.wireOp",EDGE,"E29.trimOffspring")])],"isStart":false});
            var Q36;
            Q36=makeQuery(id+"F1.opExtrude","CAP_EDGE",EDGE,{"disambiguationData":[OSD([sQuery(id+"F0.wireOp",EDGE,"E31")])],"isStart":false});
            var Q37;
            Q37=makeQuery(id+"F1.opExtrude","CAP_EDGE",EDGE,{"disambiguationData":[OSD([sQuery(id+"F0.wireOp",EDGE,"E23")])],"isStart":false});
            var Q38;
            Q38=makeQuery(id+"F1.opExtrude","CAP_EDGE",EDGE,{"disambiguationData":[OSD([sQuery(id+"F0.wireOp",EDGE,"E22")])],"isStart":false});
            var Q39;
            Q39=makeQuery(id+"F1.opExtrude","CAP_EDGE",EDGE,{"disambiguationData":[OSD([sQuery(id+"F0.wireOp",EDGE,"E24")])],"isStart":false});
            var Q40;
            Q40=makeQuery(id+"F1.opExtrude","CAP_EDGE",EDGE,{"disambiguationData":[OSD([sQuery(id+"F0.wireOp",EDGE,"E28")])],"isStart":false});
            var Q41;
            Q41=makeQuery(id+"F1.opExtrude","CAP_EDGE",EDGE,{"disambiguationData":[OSD([sQuery(id+"F0.wireOp",EDGE,"E9")])],"isStart":false});
            var Q42;
            {var subQ0=sQuery(id+"F0.wireOp",EDGE,"E1");Q42=makeQuery(id+"F1.opExtrude","CAP_EDGE",EDGE,{"disambiguationData":[OSD([subQ0]),TDD([makeQuery(id+"F0.imprint","IMPRINT",EDGE,{"disambiguationData":[TD([[makeQuery(id+"F0.imprint","INTERSECT",VERTEX,{"derivedFrom":[subQ0,sQuery(id+"F0.wireOp",EDGE,"E26.trimOffspring")]}),-1.0]])],"derivedFrom":subQ0})])],"isStart":false});}
            var Q43;
            Q43=makeQuery(id+"F1.opExtrude","CAP_EDGE",EDGE,{"disambiguationData":[OSD([sQuery(id+"F0.wireOp",EDGE,"E26.trimOffspring")])],"isStart":false});
            var Q44;
            Q44=makeQuery(id+"F1.opExtrude","CAP_EDGE",EDGE,{"disambiguationData":[OSD([sQuery(id+"F0.wireOp",EDGE,"E10")])],"isStart":false});
            var Q45;
            {var subQ0=sQuery(id+"F0.wireOp",EDGE,"E1");Q45=makeQuery(id+"F1.opExtrude","CAP_EDGE",EDGE,{"disambiguationData":[OSD([subQ0]),TDD([makeQuery(id+"F0.imprint","IMPRINT",EDGE,{"disambiguationData":[TD([[makeQuery(id+"F0.imprint","INTERSECT",VERTEX,{"disambiguationData":[OD(1.0)],"derivedFrom":[subQ0,sQuery(id+"F0.wireOp",EDGE,"E7")]}),-1.0]])],"derivedFrom":subQ0})])],"isStart":false});}
            var Q46;
            {var subQ0=sQuery(id+"F0.wireOp",EDGE,"E7");var subQ1=sQuery(id+"F0.wireOp",EDGE,"E1");Q46=makeQuery(id+"F1.opExtrude","CAP_EDGE",EDGE,{"disambiguationData":[OSD([subQ0]),TDD([makeQuery(id+"F0.imprint","IMPRINT",EDGE,{"disambiguationData":[TD([[makeQuery(id+"F0.imprint","INTERSECT",VERTEX,{"disambiguationData":[OD(0.0)],"derivedFrom":[subQ1,subQ0]}),1.0]])],"derivedFrom":subQ0})])],"isStart":false});}
            var Q47;
            {var subQ0=sQuery(id+"F0.wireOp",EDGE,"E7");Q47=makeQuery(id+"F1.opExtrude","CAP_EDGE",EDGE,{"disambiguationData":[OSD([subQ0]),TDD([makeQuery(id+"F0.imprint","IMPRINT",EDGE,{"disambiguationData":[TD([[makeQuery(id+"F0.imprint","INTERSECT",VERTEX,{"derivedFrom":[subQ0,sQuery(id+"F0.wireOp",EDGE,"E8")]}),-1.0]])],"derivedFrom":subQ0})])],"isStart":false});}
            var Q48;
            Q48=makeQuery(id+"F1.opExtrude","CAP_EDGE",EDGE,{"disambiguationData":[OSD([sQuery(id+"F0.wireOp",EDGE,"E0")])],"isStart":false});
            var Q49;
            Q49=makeQuery(id+"F1.opExtrude","CAP_EDGE",EDGE,{"disambiguationData":[OSD([sQuery(id+"F0.wireOp",EDGE,"E8")])],"isStart":false});
            var Q50;
            Q50=makeQuery(id+"F1.opExtrude","CAP_EDGE",EDGE,{"disambiguationData":[OSD([sQuery(id+"F0.wireOp",EDGE,"E8")])],"isStart":true});
            fillet(context, id + "F8", {"entities" : qUnion([Q0, Q1, Q2, Q3, Q4, Q5, Q6, Q7, Q8, Q9, Q10, Q11, Q12, Q13, Q14, Q15, Q16, Q17, Q18, Q19, Q20, Q21, Q22, Q23, Q24, Q25, Q26, Q27, Q28, Q29, Q30, Q31, Q32, Q33, Q34, Q35, Q36, Q37, Q38, Q39, Q40, Q41, Q42, Q43, Q44, Q45, Q46, Q47, Q48, Q49, Q50]), "radius" : 2.54 * mm, "tangentPropagation" : true, "allowEdgeOverflow" : false});
        }
    });
